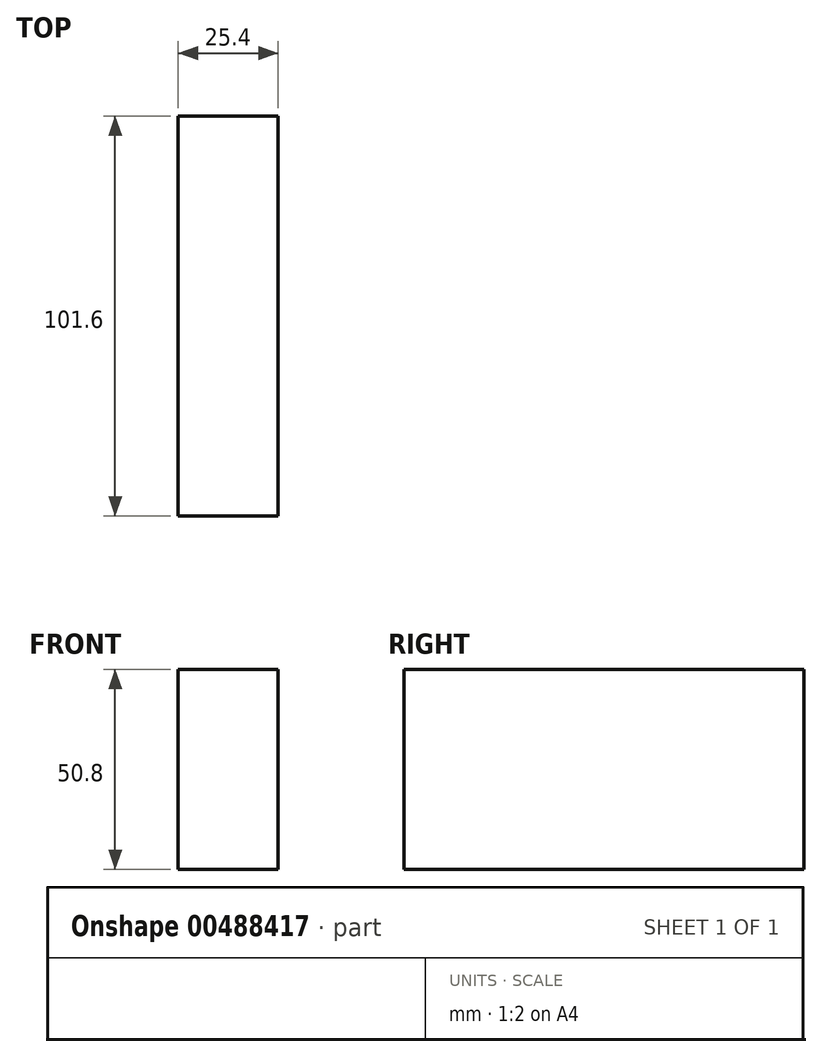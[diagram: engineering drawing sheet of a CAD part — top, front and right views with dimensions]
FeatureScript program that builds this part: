
annotation { "Feature Type Name" : "Feature", "Feature Type Description" : "" }
export const myFeature = defineFeature(function(context is Context, id is Id, definition is map)
    precondition{}
    {
        {
            var Q0;
            Q0=qCreatedBy(makeId("Front.planeOp"),FACE);
            var sketch = newSketch(context, id + "F0", { "sketchPlane" : qUnion([Q0])});
            skLineSegment(sketch, "E0.bottom", {"start": v(12.7, 25.4) * mm, "end": v(-12.7, 25.4) * mm});
            skLineSegment(sketch, "E0.top", {"start": v(12.7, -25.4) * mm, "end": v(-12.7, -25.4) * mm});
            skLineSegment(sketch, "E0.left", {"start": v(12.7, 25.4) * mm, "end": v(12.7, -25.4) * mm});
            skLineSegment(sketch, "E0.right", {"start": v(-12.7, 25.4) * mm, "end": v(-12.7, -25.4) * mm});
            skPoint(sketch, "E0.middle", {"position": v(0, 0) * mm});
            skSolve(sketch);
        }
        {
            var Q0;
            Q0 = qSketchRegion(id + "F0", true);
            extrude(context, id + "F1", {"entities" : qUnion([Q0]), "depth" : 101.6 * mm, "offsetDistance" : 25.4 * mm, "symmetric" : true});
        }
    });
